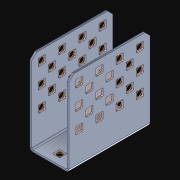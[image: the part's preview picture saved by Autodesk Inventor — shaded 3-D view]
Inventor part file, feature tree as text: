
AUTODESK INVENTOR PART (.ipt)
format: ipt  version: 2021.3 (Build 253353010, 353A)  size: 792,576 bytes
history: native  units: in
note: dims shown in document units (in); Inventor stores cm internally (conversion verified against a paired STEP export)
features: other x41, extrude x40, pattern_linear x5, sketch x2, imported_body x1
ambient origin geometry x8: Origin, YZ Plane, XZ Plane, XY Plane, X Axis, Y Axis, Z Axis, Center Point
bodies: Body1 (feature_tree), Body2 (feature_tree), Body3 (feature_tree), Body4 (feature_tree), Body5 (feature_tree), Body6 (feature_tree), Body7 (feature_tree), Body8 (feature_tree), Body9 (feature_tree), Body10 (feature_tree), Body11 (feature_tree), Body12 (feature_tree), Body13 (feature_tree), Body14 (feature_tree), Body15 (feature_tree), Body16 (feature_tree), Body17 (feature_tree), Body18 (feature_tree), Body19 (feature_tree), Body20 (feature_tree), Body21 (feature_tree), Body22 (feature_tree), Body23 (feature_tree), Body24 (feature_tree), Body25 (feature_tree), Body26 (feature_tree), Body27 (feature_tree), Body28 (feature_tree), Body29 (feature_tree), Body30 (feature_tree), Body31 (feature_tree), Body32 (feature_tree), Body33 (feature_tree), Body34 (feature_tree), Body35 (feature_tree), Body36 (feature_tree), Body37 (feature_tree), Body38 (feature_tree), Body39 (feature_tree), Body40 (feature_tree), Body41 (feature_tree)
feature tree (89):
  parser-record x1  (decoder bookkeeping rows leaked as tree rows — omitted from the tree; the rows remain in map.json)
  imported_body  "Base1"
  pattern_linear  "Rectangular Pattern1"  Count1=4 Spacing1=0.5in
  pattern_linear  "Rectangular Pattern2"  Count1=3 Spacing1=0.5in
  pattern_linear  "Rectangular Pattern3"  Spacing1=0.046in  [1 undecoded]
  pattern_linear  "Rectangular Pattern4"  Count1=3 Spacing1=0.5in
  pattern_linear  "Rectangular Pattern5"  Count1=2 Spacing1=0.5in
  other  "Srf1"
  other  "Srf2"
  other  "Srf3"
  other  "Srf4"
  other  "Srf5"
  other  "Srf6"
  other  "Srf7"
  other  "Srf8"
  other  "Srf9"
  other  "Srf10"
  other  "Srf11"
  other  "Srf12"
  sketch  "Sketch2"  dims[d40=0.046in d41=0.0in d42=1.5748in d44=0.5in d45=1.1811in d47=0.5in]
  other  "Srf13"
  other  "Srf14"
  other  "Srf15"
  other  "Srf16"
  other  "Srf17"
  other  "Srf18"
  other  "Srf19"
  other  "Srf20"
  other  "Srf21"
  other  "Srf22"
  other  "Srf23"
  other  "Srf24"
  other  "Srf25"
  other  "Srf26"
  other  "Srf27"
  other  "Srf28"
  other  "Srf29"
  other  "Srf30"
  sketch  "Sketch4"  dims[d48=0.167in d49=0.046in d50=0.0in d51=1.1811in d53=0.5in d54=0.7874in d56=0.5in d58=0.046in d59=0.0in d60=1.5748in d62=0.5in d63=1.1811in d65=0.5in d67=0.046in d68=0.0in d69=1.1811in d71=0.5in d72=0.7874in d74=0.5in d76=0.046in d77=0.0in d78=1.5748in d80=0.5in d81=0.0in d82=0.0in d83=0.0in d84=0.0in d85=0.0in d86=0.0in d87=0.0in d88=0.0in d89=0.0in d90=0.0in d91=0.0in d92=0.0in d93=0.0in d94=0.0in d95=0.0in d96=0.0in d97=0.0in d98=0.0in d99=0.0in d100=0.0in d101=0.0in d102=0.0in d103=0.0in d104=0.0in d105=0.0in d106=0.0in d107=0.0in d108=0.0in d109=0.0in d110=0.0in d111=0.0in d112=0.0in d113=0.0in d114=0.0in d115=0.0in d116=0.0in d117=0.0in d118=0.0in d119=0.0in d120=0.0in d121=0.0in d122=0.0in d123=0.0in d124=0.0in d125=0.0in d126=0.0in d127=0.0in d128=0.0in d129=0.0in d130=0.0in d131=0.0in d132=0.0in d133=0.0in d134=0.0in d135=0.0in d136=0.0in d137=0.0in d138=0.0in d139=0.0in d140=0.0in d141=0.0in d142=0.0in d143=0.0in d144=0.0in d145=0.0in d146=0.0in d147=0.0in d148=0.0in d149=0.0in d150=0.0in d151=0.0in d152=0.0in d153=0.0in d154=0.0in d155=0.0in d156=0.0in d157=0.0in d158=0.0in d159=0.0in d160=0.0in]
  other  "Srf31"
  other  "Srf32"
  other  "Srf33"
  other  "Srf34"
  other  "Srf35"
  other  "Srf36"
  other  "Srf37"
  other  "Srf38"
  other  "Srf39"
  other  "Srf40"
  extrude  "ExtrusionSrf1"  Depth=0.046in TaperAngle=0.0deg
  extrude  "ExtrusionSrf13"  Depth=0.5in
  extrude  "ExtrusionSrf19"  Depth=0.5in
  extrude  "ExtrusionSrf31"  Depth=0.046in TaperAngle=0.0deg
  extrude  "ExtrusionSrf37"  Depth=0.5in
  extrude  "ExtrusionSrf2"  Depth=0.5in
  extrude  "ExtrusionSrf3"  Depth=0.046in TaperAngle=0.0deg
  extrude  "ExtrusionSrf4"  Depth=0.5in
  extrude  "ExtrusionSrf5"  TaperAngle=0.0deg  [1 undecoded]
  extrude  "ExtrusionSrf6"  TaperAngle=0.0deg  [1 undecoded]
  extrude  "ExtrusionSrf7"  TaperAngle=0.0deg  [1 undecoded]
  extrude  "ExtrusionSrf8"  TaperAngle=0.0deg  [1 undecoded]
  extrude  "ExtrusionSrf9"  TaperAngle=0.0deg  [1 undecoded]
  extrude  "ExtrusionSrf10"  TaperAngle=0.0deg  [1 undecoded]
  extrude  "ExtrusionSrf11"  TaperAngle=0.0deg  [1 undecoded]
  extrude  "ExtrusionSrf12"  TaperAngle=0.0deg  [1 undecoded]
  extrude  "ExtrusionSrf14"  TaperAngle=0.0deg  [1 undecoded]
  extrude  "ExtrusionSrf15"  TaperAngle=0.0deg  [1 undecoded]
  extrude  "ExtrusionSrf16"  TaperAngle=0.0deg  [1 undecoded]
  extrude  "ExtrusionSrf17"  TaperAngle=0.0deg  [1 undecoded]
  extrude  "ExtrusionSrf18"  TaperAngle=0.0deg  [1 undecoded]
  extrude  "ExtrusionSrf20"  TaperAngle=0.0deg  [1 undecoded]
  extrude  "ExtrusionSrf21"  TaperAngle=0.0deg  [1 undecoded]
  extrude  "ExtrusionSrf22"  TaperAngle=0.0deg  [1 undecoded]
  extrude  "ExtrusionSrf23"  TaperAngle=0.0deg  [1 undecoded]
  extrude  "ExtrusionSrf24"  TaperAngle=0.0deg  [1 undecoded]
  extrude  "ExtrusionSrf25"  TaperAngle=0.0deg  [1 undecoded]
  extrude  "ExtrusionSrf26"  TaperAngle=0.0deg  [1 undecoded]
  extrude  "ExtrusionSrf27"  TaperAngle=0.0deg  [1 undecoded]
  extrude  "ExtrusionSrf28"  TaperAngle=0.0deg  [1 undecoded]
  extrude  "ExtrusionSrf29"  TaperAngle=0.0deg  [1 undecoded]
  extrude  "ExtrusionSrf30"  TaperAngle=0.0deg  [1 undecoded]
  extrude  "ExtrusionSrf32"  TaperAngle=0.0deg  [1 undecoded]
  extrude  "ExtrusionSrf33"  TaperAngle=0.0deg  [1 undecoded]
  extrude  "ExtrusionSrf34"  TaperAngle=0.0deg  [1 undecoded]
  extrude  "ExtrusionSrf35"  TaperAngle=0.0deg  [1 undecoded]
  extrude  "ExtrusionSrf36"  TaperAngle=0.0deg  [1 undecoded]
  extrude  "ExtrusionSrf38"  TaperAngle=0.0deg  [1 undecoded]
  extrude  "ExtrusionSrf39"  TaperAngle=0.0deg  [1 undecoded]
  extrude  "ExtrusionSrf40"  TaperAngle=0.0deg  [1 undecoded]
note: 33 required parameter values undecoded (feature->parameter linkage not recoverable at this tier; creation-order binding heuristic only, values carry confidence <= 0.55)
